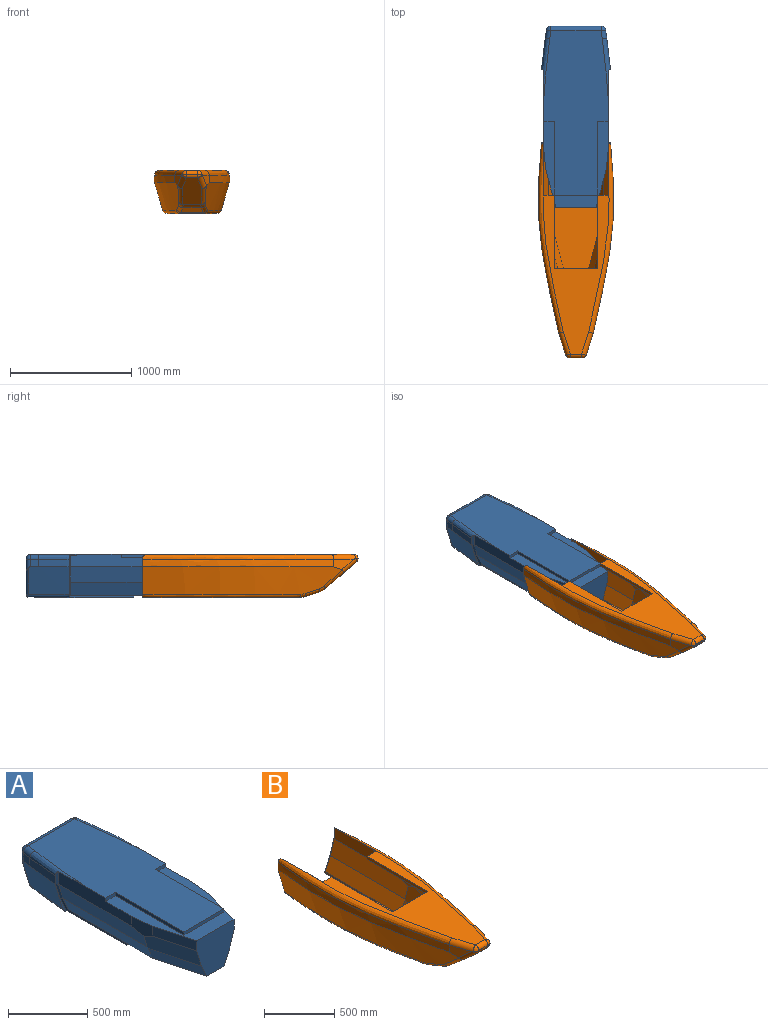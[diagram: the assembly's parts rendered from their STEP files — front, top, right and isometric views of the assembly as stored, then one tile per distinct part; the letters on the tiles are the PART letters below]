
ASSEMBLY  parts=2 mates=1
PART A: 112 faces, bbox 616.9x1608.1x392.9 mm
  f0: plane 1361.33x536.78mm, normal (0,0,1), area 586792.3mm2, adj f69,f71,f74,f76,f77,f94,f95,f96
  f1: plane 756.27x130.17mm, normal (-0.96,0,-0.29), area 98100.7mm2, adj f2,f90,f100,f104,f110
  f2: plane 382.05x139.92mm, normal (-0.93,-0.25,-0.29), area 55744.9mm2, adj f1,f5,f90,f91,f100,f103
  f3: plane 756.27x130.18mm, normal (0.96,0,-0.29), area 98100.7mm2, adj f4,f92,f101,f105,f107
  f4: plane 382.05x139.92mm, normal (0.93,-0.25,-0.29), area 55744.9mm2, adj f3,f5,f92,f93,f101,f102
  f5: plane 332.86x317.5mm, normal (0,-1,0), area 86037.5mm2, adj f2,f4,f85,f91,f93,f99,f102,f103
  f6: bspline ~581.03x256.54mm, area 79353.1mm2, adj f10,f46,f47,f70,f78,f86
  f7: bspline ~463.29x89.61mm, area 13756.4mm2, adj f8,f9,f64,f65,f79,f82,f83,f87
  f8: plane 573.52x359mm, normal (0,0,-1), area 71328.5mm2, adj f7,f10,f14,f15,f17,f18,f20,f21
  f9: bspline ~580.35x254mm, area 79352.9mm2, adj f7,f49,f50,f73,f79,f87
  f10: bspline ~488.62x92.74mm, area 13756.4mm2, adj f6,f8,f59,f61,f78,f80,f81,f86
  f11: plane 466.24x172.98mm, normal (-0.99,0,-0.14), area 66294.3mm2, adj f51,f56,f58,f81
  f12: plane 466.24x172.98mm, normal (0.99,0,-0.14), area 66294.3mm2, adj f51,f56,f62,f83
  f13: plane 266.7x6.35mm, normal (0,0,1), area 1693.5mm2, adj f14,f15,f55,f57
  f14: plane 279.4x12.7mm, normal (1,0,0), area 3467.7mm2, adj f8,f13,f55,f57
  f15: plane 279.4x12.7mm, normal (-1,0,0), area 3467.7mm2, adj f8,f13,f55,f57
  f16: plane 266.7x6.35mm, normal (0,0,1), area 1693.5mm2, adj f17,f18,f55,f57
  f17: plane 279.4x12.7mm, normal (1,0,0), area 3467.7mm2, adj f8,f16,f55,f57
  f18: plane 279.4x12.7mm, normal (-1,0,0), area 3467.7mm2, adj f8,f16,f55,f57
  f19: plane 266.7x6.35mm, normal (0,0,1), area 1693.5mm2, adj f20,f21,f55,f57
  f20: plane 279.4x12.7mm, normal (1,0,0), area 3467.7mm2, adj f8,f19,f55,f57
  f21: plane 279.4x12.7mm, normal (-1,0,0), area 3467.7mm2, adj f8,f19,f55,f57
  f22: plane 266.7x6.35mm, normal (0,0,1), area 1693.5mm2, adj f23,f24,f55,f57
  f23: plane 279.4x12.7mm, normal (1,0,0), area 3467.7mm2, adj f8,f22,f55,f57
  f24: plane 279.4x12.7mm, normal (-1,0,0), area 3467.7mm2, adj f8,f22,f55,f57
  f25: plane 266.7x6.35mm, normal (0,0,1), area 1693.5mm2, adj f26,f27,f55,f57
  f26: plane 279.4x12.7mm, normal (1,0,0), area 3467.7mm2, adj f8,f25,f55,f57
  f27: plane 279.4x12.7mm, normal (-1,0,0), area 3467.7mm2, adj f8,f25,f55,f57
  f28: plane 266.7x6.35mm, normal (0,0,1), area 1693.5mm2, adj f29,f30,f55,f57
  f29: plane 279.4x12.7mm, normal (1,0,0), area 3467.7mm2, adj f8,f28,f55,f57
  f30: plane 279.4x12.7mm, normal (-1,0,0), area 3467.7mm2, adj f8,f28,f55,f57
  f31: plane 266.7x6.35mm, normal (0,0,1), area 1693.5mm2, adj f32,f33,f55,f57
  f32: plane 279.4x12.7mm, normal (1,0,0), area 3467.7mm2, adj f8,f31,f55,f57
  f33: plane 279.4x12.7mm, normal (-1,0,0), area 3467.7mm2, adj f8,f31,f55,f57
  f34: plane 266.7x6.35mm, normal (0,0,1), area 1693.5mm2, adj f35,f36,f55,f57
  f35: plane 279.4x12.7mm, normal (1,0,0), area 3467.7mm2, adj f8,f34,f55,f57
  f36: plane 279.4x12.7mm, normal (-1,0,0), area 3467.7mm2, adj f8,f34,f55,f57
  f37: plane 266.81x6.46mm, normal (0,0,1), area 1693.2mm2, adj f38,f39,f55,f57,f68
  f38: plane 279.36x12.73mm, normal (1,0,0), area 3465.5mm2, adj f8,f37,f57,f68
  f39: plane 279.4x12.7mm, normal (-1,0,0), area 3467.7mm2, adj f8,f37,f55,f57
  f40: plane 266.74x6.39mm, normal (0,0,1), area 1693.5mm2, adj f41,f42,f55,f57,f66
  f41: plane 279.4x12.7mm, normal (1,0,0), area 3467.7mm2, adj f8,f40,f55,f57
  f42: plane 279.41x12.71mm, normal (-1,0,0), area 3467.1mm2, adj f8,f40,f57,f66
  f43: plane 266.7x6.35mm, normal (0,0,1), area 1693.5mm2, adj f44,f45,f55,f57
  f44: plane 279.4x12.7mm, normal (1,0,0), area 3467.7mm2, adj f8,f43,f55,f57
  f45: plane 279.4x12.7mm, normal (-1,0,0), area 3467.7mm2, adj f8,f43,f55,f57
  f46: extruded ~254x63.5mm, area 16237mm2, adj f6,f47,f69,f86
  f47: plane 77.21x73.17mm, normal (0.99,0.13,0), area 4434.1mm2, adj f6,f46,f70,f71
  f48: plane 415.72x263.21mm, normal (0,1,0), area 95435.2mm2, adj f61,f63,f64,f70,f73,f74,f78,f79
  f49: plane 68.46x65.05mm, normal (-0.99,0.13,0), area 4435.5mm2, adj f9,f50,f73,f76
  f50: extruded ~254x63.5mm, area 16237mm2, adj f9,f49,f77,f87
  f51: cylinder r=127mm len=370.62mm, axis (0,1,0), area 104993.5mm2, adj f11,f12,f52,f53,f56,f57,f60,f67
  f52: plane 246.91x194.95mm, normal (-0.99,0,-0.14), area 29401mm2, adj f8,f51,f57,f68
  f53: plane 246.91x194.95mm, normal (0.99,0,-0.14), area 29401mm2, adj f8,f51,f57,f66
  f54: plane 243.15x241.3mm, normal (0,-0.71,-0.71), area 67220.1mm2, adj f58,f60,f62,f63
  f55: plane 297.36x297.36mm, normal (0,0.71,-0.71), area 85914mm2, adj f8,f13,f14,f15,f16,f17,f18,f19
  f56: plane 349.15x194.95mm, normal (0,1,0), area 24764.4mm2, adj f8,f11,f12,f51,f81,f83
  f57: plane 304.8x194.95mm, normal (0,-1,0), area 23677mm2, adj f8,f13,f14,f15,f16,f17,f18,f19
  f58: cylinder r=25.4mm len=198.95mm, axis (-0.1,-0.7,0.7), area 8832.8mm2, adj f11,f54,f60,f61,f80
  f59: cylinder r=25.4mm len=8.2mm, axis (0.14,0,-0.99), area 10.5mm2, adj f10,f61,f80
  f60: bspline ~252.55x113.17mm, area 10416.1mm2, adj f51,f54,f58,f62
  f61: bspline ~68.41x55.23mm, area 2829.9mm2, adj f10,f48,f58,f59,f63,f78,f80
  f62: cylinder r=25.4mm len=198.95mm, axis (0.1,-0.7,0.7), area 8832.8mm2, adj f12,f54,f60,f64,f82
  f63: cylinder r=25.4mm len=243.15mm, axis (1,0,0), area 14551.7mm2, adj f48,f54,f61,f64
  f64: bspline ~68.41x55.23mm, area 2829.9mm2, adj f7,f48,f62,f63,f65,f79,f82
  f65: cylinder r=25.4mm len=8.2mm, axis (0.14,0,0.99), area 10.5mm2, adj f7,f64,f82
  f66: cylinder r=25.4mm len=227.53mm, axis (-0.1,-0.7,-0.7), area 10875.4mm2, adj f8,f40,f42,f53,f55,f67
  f67: bspline ~251.67x109.8mm, area 10416.1mm2, adj f51,f55,f66,f68
  f68: cylinder r=25.4mm len=227.52mm, axis (0.1,-0.7,-0.7), area 10852.3mm2, adj f8,f37,f38,f52,f55,f67
  f69: bspline ~506.89x87.96mm, area 18013.5mm2, adj f0,f46,f71,f86,f105,f106
  f70: cylinder r=38.1mm len=98.43mm, axis (0,0,-1), area 4456.1mm2, adj f6,f47,f48,f72,f78
  f71: cylinder r=38.1mm len=73.38mm, axis (0.13,-0.99,0), area 4127mm2, adj f0,f47,f69,f72
  f72: sphere r=38.1mm, area 1331.5mm2, adj f70,f71,f74
  f73: cylinder r=38.1mm len=98.43mm, axis (0,0,1), area 4456.1mm2, adj f9,f48,f49,f75,f79
  f74: cylinder r=38.1mm len=415.72mm, axis (1,0,0), area 24879.4mm2, adj f0,f48,f72,f75
  f75: sphere r=38.1mm, area 2920mm2, adj f73,f74,f76
  f76: cylinder r=38.1mm len=73.38mm, axis (0.13,0.99,0), area 4127mm2, adj f0,f49,f75,f77
  f77: bspline ~506.89x87.96mm, area 18012.6mm2, adj f0,f50,f76,f87,f104,f109
  f78: bspline ~314.62x117.05mm, area 8046.9mm2, adj f6,f10,f48,f61,f70
  f79: bspline ~311.61x116.14mm, area 8046.9mm2, adj f7,f9,f48,f64,f73
  f80: bspline ~48.73x28.88mm, area 378.3mm2, adj f10,f58,f59,f61,f81
  f81: cylinder r=25.4mm len=466.24mm, axis (0,-1,0), area 14881.2mm2, adj f8,f10,f11,f56,f80
  f82: bspline ~48.73x28.88mm, area 378.3mm2, adj f7,f62,f64,f65,f83
  f83: cylinder r=25.4mm len=466.24mm, axis (0,1,0), area 14881.2mm2, adj f7,f8,f12,f56,f82
  f84: plane 355.6x12.7mm, normal (0,-1,0), area 4516.1mm2, adj f8,f85,f88,f89
  f85: plane 609.6x355.6mm, normal (0,0,-1), area 178064.2mm2, adj f5,f84,f90,f91,f92,f93
  f86: plane 335.98x98.74mm, normal (0,-1,0), area 2252.6mm2, adj f6,f10,f46,f69,f106,f107,f108
  f87: plane 336.02x98.78mm, normal (0,-1,0), area 2252.7mm2, adj f7,f9,f50,f77,f109,f110,f111
  f88: plane 525.86x12.7mm, normal (1,0,0), area 6645.6mm2, adj f8,f84,f92,f108
  f89: plane 525.86x12.7mm, normal (-1,0,0), area 6645.6mm2, adj f8,f84,f90,f111
  f90: plane 755.27x114.3mm, normal (-0.91,0,-0.41), area 94095.9mm2, adj f1,f2,f85,f89,f91,f111
  f91: plane 381x147.12mm, normal (-0.88,-0.24,-0.41), area 43850.9mm2, adj f2,f5,f85,f90
  f92: plane 755.27x114.3mm, normal (0.91,0,-0.41), area 94095.9mm2, adj f3,f4,f85,f88,f93,f108
  f93: plane 381x147.12mm, normal (0.88,-0.24,-0.41), area 43850.9mm2, adj f4,f5,f85,f92
  f94: plane 88.9x25.4mm, normal (0,-1,0), area 2258.1mm2, adj f0,f95,f99,f105
  f95: plane 609.6x25.4mm, normal (1,0,0), area 15483.8mm2, adj f0,f94,f96,f99
  f96: plane 355.6x25.4mm, normal (0,-1,0), area 9032.2mm2, adj f0,f95,f97,f99
  f97: plane 609.6x25.4mm, normal (-1,0,0), area 15483.8mm2, adj f0,f96,f98,f99
  f98: plane 88.9x25.4mm, normal (0,-1,0), area 2258.1mm2, adj f0,f97,f99,f104
  f99: plane 712.19x534.39mm, normal (0,0,1), area 123369.8mm2, adj f5,f94,f95,f96,f97,f98,f100,f101
  f100: extruded ~169.31x107.19mm, area 15605.5mm2, adj f1,f2,f99,f103,f104
  f101: extruded ~169.31x107.19mm, area 15605.7mm2, adj f3,f4,f99,f102,f105
  f102: plane 311.96x83.19mm, normal (0.97,-0.26,0), area 24602.2mm2, adj f4,f5,f99,f101
  f103: plane 311.96x83.19mm, normal (-0.97,-0.26,0), area 24602.2mm2, adj f2,f5,f99,f100
  f104: plane 651.76x104.33mm, normal (-1,0,0), area 59731.6mm2, adj f0,f1,f77,f98,f99,f100,f109
  f105: plane 651.79x104.36mm, normal (1,0,0), area 59731.6mm2, adj f0,f3,f69,f94,f99,f101,f106
  f106: plane 99.47x14.14mm, normal (0.71,-0.71,0), area 1636.6mm2, adj f69,f86,f105,f107
  f107: plane 131.42x50.8mm, normal (0.68,-0.71,-0.2), area 2405.4mm2, adj f3,f86,f106,f108
  f108: plane 127.12x62.85mm, normal (0.65,-0.71,-0.29), area 2399.8mm2, adj f8,f10,f86,f88,f92,f107
  f109: plane 99.46x14.13mm, normal (-0.71,-0.71,0), area 1636.6mm2, adj f77,f87,f104,f110
  f110: plane 131.42x50.8mm, normal (-0.68,-0.71,-0.2), area 2405.4mm2, adj f1,f87,f109,f111
  f111: plane 127.12x62.85mm, normal (-0.65,-0.71,-0.29), area 2399.8mm2, adj f7,f8,f87,f89,f90,f110
PART B: 68 faces, bbox 626.9x1864.8x376.1 mm
  f0: bspline ~1752.75x265.7mm, area 366475.3mm2, adj f1,f8,f13,f14,f15,f16,f25,f28
  f1: extruded ~1574.8x169.81mm, area 101050.6mm2, adj f0,f5,f8,f42
  f2: extruded ~1574.8x169.81mm, area 101050.6mm2, adj f6,f7,f9,f43
  f3: plane 1497.26x549.49mm, normal (0,0,1), area 290140.1mm2, adj f5,f6,f17,f21,f33,f50,f51,f52
  f4: plane 1290.15x413.65mm, normal (0,0,-1), area 271720.8mm2, adj f13,f18,f24,f40,f44,f45,f64,f67
  f5: bspline ~1575.27x207.08mm, area 92192.4mm2, adj f1,f3,f17,f42,f61,f62
  f6: bspline ~1575.27x207.09mm, area 92193mm2, adj f2,f3,f21,f43,f60,f65
  f7: bspline ~1752.78x264.95mm, area 366474.7mm2, adj f2,f9,f18,f19,f20,f22,f23,f26
  f8: plane 171.21x87.22mm, normal (0.95,-0.31,0), area 10169.1mm2, adj f0,f1,f16,f17
  f9: plane 171.21x87.22mm, normal (-0.95,-0.31,0), area 10169.1mm2, adj f2,f7,f21,f22
  f10: plane 103.3x4.48mm, normal (0,-1,0), area 450.5mm2, adj f29,f30,f31,f32,f33,f34
  f11: plane 179.8x116.12mm, normal (0,-0.32,-0.95), area 20301.8mm2, adj f14,f19,f24,f27
  f12: plane 255.38x219.72mm, normal (0,-0.65,-0.76), area 48649.2mm2, adj f15,f16,f20,f22,f27,f30
  f13: bspline ~1398.53x156.89mm, area 63886.3mm2, adj f0,f4,f25,f42,f64
  f14: bspline ~212.58x93.67mm, area 5753.1mm2, adj f0,f11,f25,f28
  f15: bspline ~205.58x180.79mm, area 9341.5mm2, adj f0,f12,f16,f28
  f16: cylinder r=38.1mm len=124.95mm, axis (-0.24,-0.74,0.63), area 7553.8mm2, adj f0,f8,f12,f15,f17,f32,f34
  f17: cylinder r=38.1mm len=194.75mm, axis (-0.31,-0.95,0), area 11369.8mm2, adj f3,f5,f8,f16,f34
  f18: bspline ~1393.26x155.58mm, area 63886.2mm2, adj f4,f7,f23,f43,f67
  f19: bspline ~165.53x78.02mm, area 5753.2mm2, adj f7,f11,f23,f26
  f20: bspline ~203.71x179.17mm, area 9341.5mm2, adj f7,f12,f22,f26
  f21: cylinder r=38.1mm len=194.75mm, axis (-0.31,0.95,0), area 11369.8mm2, adj f3,f6,f9,f22,f31
  f22: cylinder r=38.1mm len=124.95mm, axis (0.24,-0.74,0.63), area 7553.8mm2, adj f7,f9,f12,f20,f21,f29,f31
  f23: bspline ~73.08x44.43mm, area 2110.6mm2, adj f7,f18,f19,f24
  f24: cylinder r=152.4mm len=192.14mm, axis (1,0,0), area 9118.8mm2, adj f4,f11,f23,f25
  f25: bspline ~72.95x44.33mm, area 2110.5mm2, adj f0,f13,f14,f24
  f26: bspline ~66.87x53.1mm, area 2447.2mm2, adj f7,f19,f20,f27
  f27: cylinder r=152.4mm len=151.9mm, axis (1,0,0), area 8891.1mm2, adj f11,f12,f26,f28
  f28: bspline ~75.37x58.74mm, area 2447.2mm2, adj f0,f14,f15,f27
  f29: bspline ~41.81x31.08mm, area 770.8mm2, adj f10,f22,f30,f31
  f30: cylinder r=31.75mm len=95.42mm, axis (-1,0,0), area 2606.4mm2, adj f10,f12,f29,f32
  f31: bspline ~37.48x36.72mm, area 1551.2mm2, adj f10,f21,f22,f29,f33
  f32: bspline ~41.81x31.08mm, area 770.8mm2, adj f10,f16,f30,f34
  f33: cylinder r=31.75mm len=92.76mm, axis (-1,0,0), area 4626.2mm2, adj f3,f10,f31,f34
  f34: bspline ~37.48x36.72mm, area 1551.2mm2, adj f10,f16,f17,f32,f33
  f35: plane 756.27x130.17mm, normal (0.96,0,0.29), area 98100.7mm2, adj f36,f46,f56,f60,f66
  f36: plane 382.05x139.92mm, normal (0.93,0.25,0.29), area 55744.9mm2, adj f35,f39,f46,f47,f56,f59
  f37: plane 756.27x130.18mm, normal (-0.96,0,0.29), area 98100.7mm2, adj f38,f48,f57,f61,f63
  f38: plane 382.05x139.92mm, normal (-0.93,0.25,0.29), area 55744.9mm2, adj f37,f39,f48,f49,f57,f58
  f39: plane 332.86x317.5mm, normal (0,1,0), area 86037.5mm2, adj f36,f38,f41,f47,f49,f55,f58,f59
  f40: plane 355.6x12.7mm, normal (0,1,0), area 4516.1mm2, adj f4,f41,f44,f45
  f41: plane 609.6x355.6mm, normal (0,0,1), area 178064.2mm2, adj f39,f40,f46,f47,f48,f49
  f42: plane 335.98x98.74mm, normal (0,1,0), area 2252.6mm2, adj f0,f1,f5,f13,f62,f63,f64
  f43: plane 336.02x98.78mm, normal (0,1,0), area 2252.7mm2, adj f2,f6,f7,f18,f65,f66,f67
  f44: plane 525.86x12.7mm, normal (-1,0,0), area 6645.6mm2, adj f4,f40,f48,f64
  f45: plane 525.86x12.7mm, normal (1,0,0), area 6645.6mm2, adj f4,f40,f46,f67
  f46: plane 755.27x114.3mm, normal (0.91,0,0.41), area 94095.9mm2, adj f35,f36,f41,f45,f47,f67
  f47: plane 381x147.12mm, normal (0.88,0.24,0.41), area 43850.9mm2, adj f36,f39,f41,f46
  f48: plane 755.27x114.3mm, normal (-0.91,0,0.41), area 94095.9mm2, adj f37,f38,f41,f44,f49,f64
  f49: plane 381x147.12mm, normal (-0.88,0.24,0.41), area 43850.9mm2, adj f38,f39,f41,f48
  f50: plane 88.9x25.4mm, normal (0,1,0), area 2258.1mm2, adj f3,f51,f55,f61
  f51: plane 609.6x25.4mm, normal (-1,0,0), area 15483.8mm2, adj f3,f50,f52,f55
  f52: plane 355.6x25.4mm, normal (0,1,0), area 9032.2mm2, adj f3,f51,f53,f55
  f53: plane 609.6x25.4mm, normal (1,0,0), area 15483.8mm2, adj f3,f52,f54,f55
  f54: plane 88.9x25.4mm, normal (0,1,0), area 2258.1mm2, adj f3,f53,f55,f60
  f55: plane 712.19x534.39mm, normal (0,0,-1), area 123369.8mm2, adj f39,f50,f51,f52,f53,f54,f56,f57
  f56: extruded ~169.31x107.19mm, area 15605.5mm2, adj f35,f36,f55,f59,f60
  f57: extruded ~169.31x107.19mm, area 15605.7mm2, adj f37,f38,f55,f58,f61
  f58: plane 311.96x83.19mm, normal (-0.97,0.26,0), area 24602.2mm2, adj f38,f39,f55,f57
  f59: plane 311.96x83.19mm, normal (0.97,0.26,0), area 24602.2mm2, adj f36,f39,f55,f56
  f60: plane 651.76x104.33mm, normal (1,0,0), area 59731.6mm2, adj f3,f6,f35,f54,f55,f56,f65
  f61: plane 651.79x104.36mm, normal (-1,0,0), area 59731.6mm2, adj f3,f5,f37,f50,f55,f57,f62
  f62: plane 99.47x14.14mm, normal (-0.71,0.71,0), area 1636.6mm2, adj f5,f42,f61,f63
  f63: plane 131.42x50.8mm, normal (-0.68,0.71,0.2), area 2405.4mm2, adj f37,f42,f62,f64
  f64: plane 127.12x62.85mm, normal (-0.65,0.71,0.29), area 2399.8mm2, adj f4,f13,f42,f44,f48,f63
  f65: plane 99.46x14.13mm, normal (0.71,0.71,0), area 1636.6mm2, adj f6,f43,f60,f66
  f66: plane 131.42x50.8mm, normal (0.68,0.71,0.2), area 2405.4mm2, adj f35,f43,f65,f67
  f67: plane 127.12x62.85mm, normal (0.65,0.71,0.29), area 2399.8mm2, adj f4,f18,f43,f45,f46,f66
PLACE A t=(0,776.66,0)mm
PLACE B t=(0,167.06,0)mm
MATE slider A.f5 <-> B.f39  axis (0,-1,0) through (0,294.06,330.2)mm
